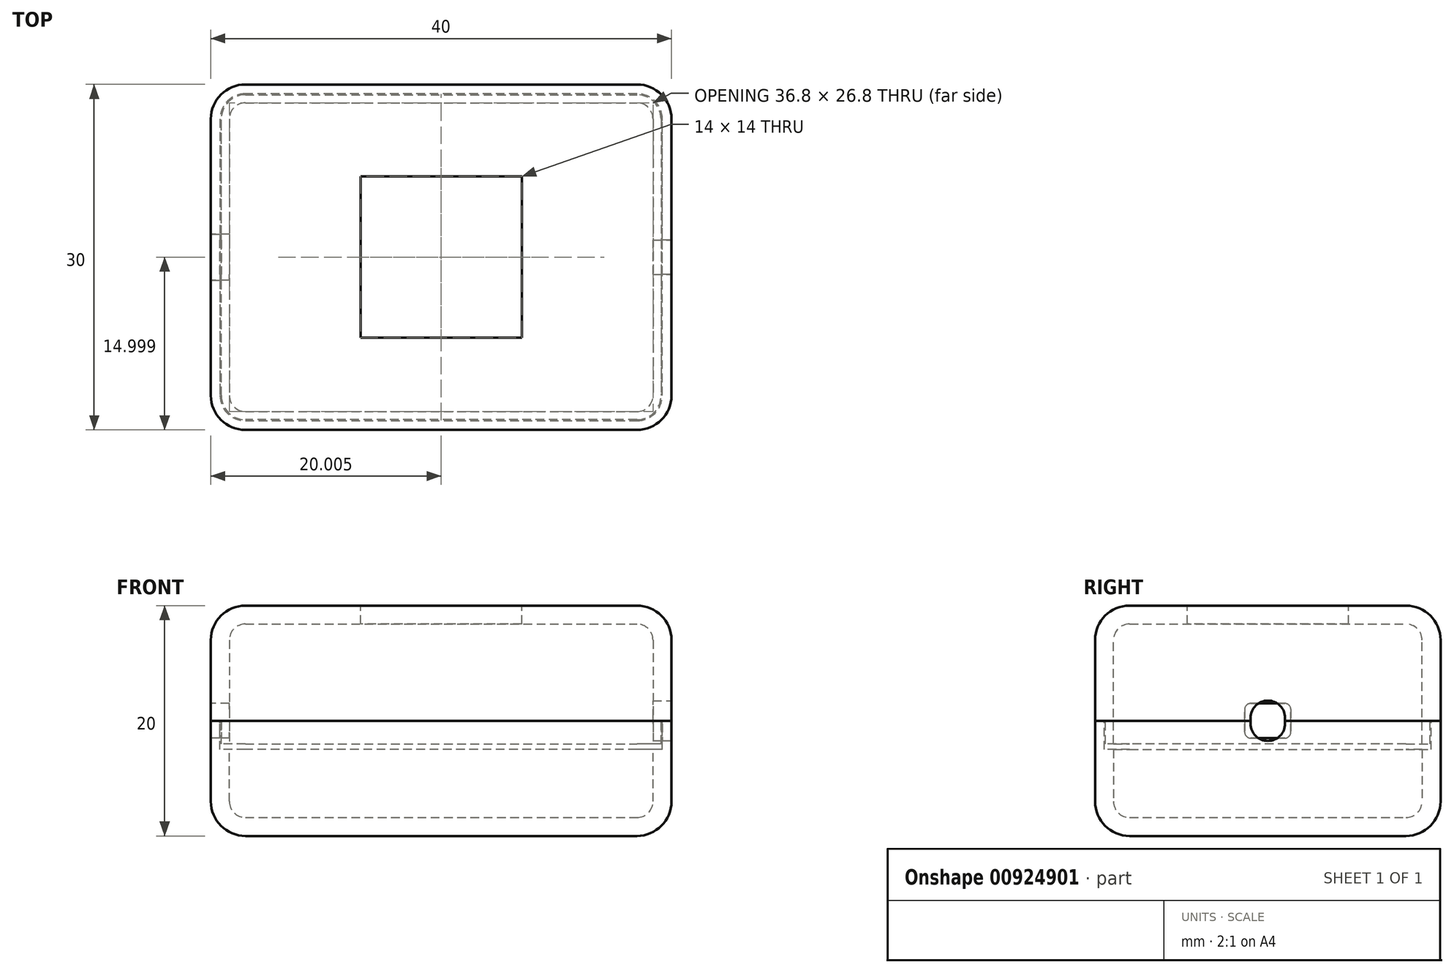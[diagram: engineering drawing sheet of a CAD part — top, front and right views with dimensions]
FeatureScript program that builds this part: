
annotation { "Feature Type Name" : "Feature", "Feature Type Description" : "" }
export const myFeature = defineFeature(function(context is Context, id is Id, definition is map)
    precondition{}
    {
        {
            var Q0;
            Q0=qCreatedBy(makeId("Top.planeOp"),FACE);
            var sketch = newSketch(context, id + "F0", { "sketchPlane" : qUnion([Q0])});
            skLineSegment(sketch, "E0.bottom", {"start": v(-19.45, 19.38) * mm, "end": v(20.55, 19.38) * mm});
            skLineSegment(sketch, "E0.top", {"start": v(-19.45, -10.62) * mm, "end": v(20.55, -10.62) * mm});
            skLineSegment(sketch, "E0.left", {"start": v(-19.45, 19.38) * mm, "end": v(-19.45, -10.62) * mm});
            skLineSegment(sketch, "E0.right", {"start": v(20.55, 19.38) * mm, "end": v(20.55, -10.62) * mm});
            skSolve(sketch);
        }
        {
            var Q0;
            Q0=makeQuery(id+"F0.imprint","IMPRINT",FACE,{"disambiguationData":[TD([[makeQuery(id+"F0.imprint","IMPRINT",EDGE,{"derivedFrom":sQuery(id+"F0.wireOp",EDGE,"6f73b4d0-b99c-471a-bee1-44a85ac8f1db.0")}),1.0]])]});
            var Q1;
            Q1=makeQuery(id+"F0.imprint","IMPRINT",FACE,{"disambiguationData":[TD([[makeQuery(id+"F0.imprint","IMPRINT",EDGE,{"derivedFrom":sQuery(id+"F0.wireOp",EDGE,"E0.bottom")}),-1.0]])]});
            extrude(context, id + "F1", {"entities" : qUnion([Q0, Q1]), "depth" : 10 * mm, "offsetDistance" : 25 * mm});
        }
        {
            var Q0;
            Q0=makeQuery(id+"F1.opExtrude","CAP_FACE",FACE,{"disambiguationData":[OSD([sQuery(id+"F0.wireOp",EDGE,"E0.bottom"),sQuery(id+"F0.wireOp",EDGE,"E0.top"),sQuery(id+"F0.wireOp",EDGE,"E0.left"),sQuery(id+"F0.wireOp",EDGE,"E0.right")])],"isStart":true});
            extrude(context, id + "F2", {"entities" : qUnion([Q0]), "depth" : 10 * mm, "offsetDistance" : 25 * mm});
        }
        {
            var Q0;
            Q0=makeQuery(id+"F2.opExtrude","SWEPT_EDGE",EDGE,{"disambiguationData":[OSD([sQuery(id+"F0.wireOp",EDGE,"E0.top"),sQuery(id+"F0.wireOp",EDGE,"E0.left")])]});
            var Q1;
            Q1=makeQuery(id+"F1.opExtrude","SWEPT_EDGE",EDGE,{"disambiguationData":[OSD([sQuery(id+"F0.wireOp",EDGE,"E0.top"),sQuery(id+"F0.wireOp",EDGE,"E0.left")])]});
            var Q2;
            Q2=makeQuery(id+"F2.opExtrude","SWEPT_EDGE",EDGE,{"disambiguationData":[OSD([sQuery(id+"F0.wireOp",EDGE,"E0.top"),sQuery(id+"F0.wireOp",EDGE,"E0.right")])]});
            var Q3;
            Q3=makeQuery(id+"F1.opExtrude","SWEPT_EDGE",EDGE,{"disambiguationData":[OSD([sQuery(id+"F0.wireOp",EDGE,"E0.top"),sQuery(id+"F0.wireOp",EDGE,"E0.right")])]});
            var Q4;
            Q4=makeQuery(id+"F2.opExtrude","SWEPT_EDGE",EDGE,{"disambiguationData":[OSD([sQuery(id+"F0.wireOp",EDGE,"E0.bottom"),sQuery(id+"F0.wireOp",EDGE,"E0.right")])]});
            var Q5;
            Q5=makeQuery(id+"F1.opExtrude","SWEPT_EDGE",EDGE,{"disambiguationData":[OSD([sQuery(id+"F0.wireOp",EDGE,"E0.bottom"),sQuery(id+"F0.wireOp",EDGE,"E0.right")])]});
            var Q6;
            Q6=makeQuery(id+"F2.opExtrude","SWEPT_EDGE",EDGE,{"disambiguationData":[OSD([sQuery(id+"F0.wireOp",EDGE,"E0.bottom"),sQuery(id+"F0.wireOp",EDGE,"E0.left")])]});
            var Q7;
            Q7=makeQuery(id+"F1.opExtrude","SWEPT_EDGE",EDGE,{"disambiguationData":[OSD([sQuery(id+"F0.wireOp",EDGE,"E0.bottom"),sQuery(id+"F0.wireOp",EDGE,"E0.left")])]});
            var Q8;
            Q8=makeQuery(id+"F2.opExtrude","CAP_EDGE",EDGE,{"disambiguationData":[OSD([sQuery(id+"F0.wireOp",EDGE,"E0.bottom")])],"isStart":false});
            var Q9;
            Q9=makeQuery(id+"F2.opExtrude","CAP_EDGE",EDGE,{"disambiguationData":[OSD([sQuery(id+"F0.wireOp",EDGE,"E0.left")])],"isStart":false});
            var Q10;
            Q10=makeQuery(id+"F2.opExtrude","CAP_EDGE",EDGE,{"disambiguationData":[OSD([sQuery(id+"F0.wireOp",EDGE,"E0.top")])],"isStart":false});
            var Q11;
            Q11=makeQuery(id+"F2.opExtrude","CAP_EDGE",EDGE,{"disambiguationData":[OSD([sQuery(id+"F0.wireOp",EDGE,"E0.right")])],"isStart":false});
            var Q12;
            Q12=makeQuery(id+"F1.opExtrude","CAP_EDGE",EDGE,{"disambiguationData":[OSD([sQuery(id+"F0.wireOp",EDGE,"E0.right")])],"isStart":false});
            var Q13;
            Q13=makeQuery(id+"F1.opExtrude","CAP_EDGE",EDGE,{"disambiguationData":[OSD([sQuery(id+"F0.wireOp",EDGE,"E0.bottom")])],"isStart":false});
            var Q14;
            Q14=makeQuery(id+"F1.opExtrude","CAP_FACE",FACE,{"disambiguationData":[OSD([sQuery(id+"F0.wireOp",EDGE,"E0.bottom"),sQuery(id+"F0.wireOp",EDGE,"E0.top"),sQuery(id+"F0.wireOp",EDGE,"E0.left"),sQuery(id+"F0.wireOp",EDGE,"E0.right")])],"isStart":false});
            fillet(context, id + "F3", {"entities" : qUnion([Q0, Q1, Q2, Q3, Q4, Q5, Q6, Q7, Q8, Q9, Q10, Q11, Q12, Q13, Q14]), "radius" : 3 * mm, "tangentPropagation" : true, "allowEdgeOverflow" : false});
        }
        {
            var Q0;
            Q0=makeQuery(id+"F2.opExtrude","CAP_FACE",FACE,{"disambiguationData":[OSD([sQuery(id+"F0.wireOp",EDGE,"E0.bottom"),sQuery(id+"F0.wireOp",EDGE,"E0.top"),sQuery(id+"F0.wireOp",EDGE,"E0.left"),sQuery(id+"F0.wireOp",EDGE,"E0.right")])],"isStart":true});
            shell(context, id + "F4", {"entities" : qUnion([Q0]), "thickness" : 1.6 * mm});
        }
        {
            var Q0;
            Q0=makeQuery(id+"F1.opExtrude","CAP_FACE",FACE,{"disambiguationData":[OSD([sQuery(id+"F0.wireOp",EDGE,"E0.bottom"),sQuery(id+"F0.wireOp",EDGE,"E0.top"),sQuery(id+"F0.wireOp",EDGE,"E0.left"),sQuery(id+"F0.wireOp",EDGE,"E0.right")])],"isStart":true});
            shell(context, id + "F5", {"entities" : qUnion([Q0]), "thickness" : 1.6 * mm});
        }
        {
            var Q0;
            Q0=makeQuery(id+"F1.opExtrude","CAP_FACE",FACE,{"disambiguationData":[OSD([sQuery(id+"F0.wireOp",EDGE,"E0.bottom"),sQuery(id+"F0.wireOp",EDGE,"E0.top"),sQuery(id+"F0.wireOp",EDGE,"E0.left"),sQuery(id+"F0.wireOp",EDGE,"E0.right")])],"isStart":false});
            var sketch = newSketch(context, id + "F6", { "sketchPlane" : qUnion([Q0])});
            skLineSegment(sketch, "E1.bottom", {"start": v(7.55, 11.38) * mm, "end": v(-6.45, 11.38) * mm});
            skLineSegment(sketch, "E1.top", {"start": v(7.55, -2.62) * mm, "end": v(-6.45, -2.62) * mm});
            skLineSegment(sketch, "E1.left", {"start": v(7.55, 11.38) * mm, "end": v(7.55, -2.62) * mm});
            skLineSegment(sketch, "E1.right", {"start": v(-6.45, 11.38) * mm, "end": v(-6.45, -2.62) * mm});
            skPoint(sketch, "E1.middle", {"position": v(0.55, 4.38) * mm});
            skPoint(sketch, "E1.middle.positionSnap0", {"position": v(17.55, 4.38) * mm});
            skPoint(sketch, "E1.middle.positionSnap1", {"position": v(0.55, 16.38) * mm});
            skPoint(sketch, "E1.centerSnap0", {"position": v(17.55, 4.38) * mm});
            skPoint(sketch, "E1.centerSnap1", {"position": v(0.55, 16.38) * mm});
            skSolve(sketch);
        }
        {
            var Q0;
            Q0=makeQuery(id+"F6.imprint","IMPRINT",FACE,{"disambiguationData":[TD([[makeQuery(id+"F6.imprint","IMPRINT",EDGE,{"derivedFrom":sQuery(id+"F6.wireOp",EDGE,"E1.bottom")}),1.0]])]});
            extrude(context, id + "F7", {"entities" : qUnion([Q0]), "operationType" : NewBodyOperationType.REMOVE, "oppositeDirection" : true, "depth" : 3 * mm, "offsetDistance" : 25 * mm});
        }
        {
            var Q0;
            Q0=makeQuery(id+"F2.opExtrude","CAP_FACE",FACE,{"disambiguationData":[OSD([sQuery(id+"F0.wireOp",EDGE,"E0.bottom"),sQuery(id+"F0.wireOp",EDGE,"E0.top"),sQuery(id+"F0.wireOp",EDGE,"E0.left"),sQuery(id+"F0.wireOp",EDGE,"E0.right")])],"isStart":true});
            var sketch = newSketch(context, id + "F8", { "sketchPlane" : qUnion([Q0])});
            skArc(sketch, "E2.0", {"start": v(19.75, 16.38) * mm, "mid": v(19.11, 17.93) * mm, "end": v(17.55, 18.58) * mm});
            skLineSegment(sketch, "E2.1", {"start": v(19.75, -7.62) * mm, "end": v(19.75, 16.38) * mm});
            skLineSegment(sketch, "E2.2", {"start": v(17.55, 18.58) * mm, "end": v(-16.45, 18.58) * mm});
            skArc(sketch, "E2.3", {"start": v(17.55, -9.82) * mm, "mid": v(19.11, -9.18) * mm, "end": v(19.75, -7.62) * mm});
            skArc(sketch, "E2.4", {"start": v(-16.45, 18.58) * mm, "mid": v(-18, 17.93) * mm, "end": v(-18.65, 16.38) * mm});
            skLineSegment(sketch, "E2.5", {"start": v(-18.65, 16.38) * mm, "end": v(-18.65, -7.62) * mm});
            skArc(sketch, "E2.6", {"start": v(-18.65, -7.62) * mm, "mid": v(-18, -9.18) * mm, "end": v(-16.45, -9.82) * mm});
            skLineSegment(sketch, "E2.7", {"start": v(-16.45, -9.82) * mm, "end": v(17.55, -9.82) * mm});
            skSolve(sketch);
        }
        {
            var Q0;
            Q0=makeQuery(id+"F8.imprint","IMPRINT",FACE,{"disambiguationData":[TD([[makeQuery(id+"F8.imprint","IMPRINT",EDGE,{"derivedFrom":sQuery(id+"F8.wireOp",EDGE,"E2.0")}),1.0]])]});
            extrude(context, id + "F9", {"entities" : qUnion([Q0]), "operationType" : NewBodyOperationType.REMOVE, "oppositeDirection" : true, "depth" : 2.5 * mm, "offsetDistance" : 25 * mm});
        }
        {
            var Q0;
            Q0=makeQuery(id+"F1.opExtrude","CAP_FACE",FACE,{"disambiguationData":[OSD([sQuery(id+"F0.wireOp",EDGE,"E0.bottom"),sQuery(id+"F0.wireOp",EDGE,"E0.top"),sQuery(id+"F0.wireOp",EDGE,"E0.left"),sQuery(id+"F0.wireOp",EDGE,"E0.right")])],"isStart":true});
            var sketch = newSketch(context, id + "F10", { "sketchPlane" : qUnion([Q0])});
            skArc(sketch, "E3.0", {"start": v(19.65, 7.62) * mm, "mid": v(19.04, 9.1) * mm, "end": v(17.55, 9.72) * mm});
            skLineSegment(sketch, "E3.1", {"start": v(19.65, -16.38) * mm, "end": v(19.65, 7.62) * mm});
            skLineSegment(sketch, "E3.2", {"start": v(17.55, 9.72) * mm, "end": v(-16.45, 9.72) * mm});
            skArc(sketch, "E3.3", {"start": v(17.55, -18.48) * mm, "mid": v(19.04, -17.86) * mm, "end": v(19.65, -16.38) * mm});
            skArc(sketch, "E3.4", {"start": v(-16.45, 9.72) * mm, "mid": v(-17.93, 9.1) * mm, "end": v(-18.55, 7.62) * mm});
            skLineSegment(sketch, "E3.5", {"start": v(-18.55, 7.62) * mm, "end": v(-18.55, -16.38) * mm});
            skArc(sketch, "E3.6", {"start": v(-18.55, -16.38) * mm, "mid": v(-17.93, -17.86) * mm, "end": v(-16.45, -18.48) * mm});
            skLineSegment(sketch, "E3.7", {"start": v(-16.45, -18.48) * mm, "end": v(17.55, -18.48) * mm});
            skSolve(sketch);
        }
        {
            var Q0;
            Q0=makeQuery(id+"F10.imprint","IMPRINT",FACE,{"disambiguationData":[TD([[makeQuery(id+"F10.imprint","IMPRINT",EDGE,{"derivedFrom":sQuery(id+"F10.wireOp",EDGE,"E3.0")}),1.0]])]});
            extrude(context, id + "F11", {"entities" : qUnion([Q0]), "operationType" : NewBodyOperationType.ADD, "depth" : 2 * mm, "offsetDistance" : 25 * mm});
        }
        {
            var Q0;
            Q0=makeQuery(id+"F2.opExtrude","SWEPT_FACE",FACE,{"disambiguationData":[OSD([sQuery(id+"F0.wireOp",EDGE,"E0.left")])]});
            var sketch = newSketch(context, id + "F12", { "sketchPlane" : qUnion([Q0])});
            skPoint(sketch, "E4.middle.positionSnap0", {"position": v(7.62, -3.5) * mm});
            skPoint(sketch, "E4.middle.positionSnap1", {"position": v(-4.38, -7) * mm});
            skPoint(sketch, "E4.centerSnap0", {"position": v(7.62, -3.5) * mm});
            skPoint(sketch, "E4.centerSnap1", {"position": v(-4.38, -7) * mm});
            skPoint(sketch, "E5.middle.positionSnap0", {"position": v(-4.38, 0) * mm});
            skPoint(sketch, "E5.centerSnap0", {"position": v(-4.38, 0) * mm});
            skLineSegment(sketch, "E6.bottom", {"start": v(-2.38, -1.5) * mm, "end": v(-6.38, -1.5) * mm});
            skLineSegment(sketch, "E6.top", {"start": v(-2.38, 1.5) * mm, "end": v(-6.38, 1.5) * mm});
            skLineSegment(sketch, "E6.left", {"start": v(-2.38, -1.5) * mm, "end": v(-2.38, 1.5) * mm});
            skLineSegment(sketch, "E6.right", {"start": v(-6.38, -1.5) * mm, "end": v(-6.38, 1.5) * mm});
            skSolve(sketch);
        }
        {
            var Q0;
            {var subQ0=sQuery(id+"F12.wireOp",EDGE,"E6.bottom");Q0=makeQuery(id+"F12.imprint","IMPRINT",FACE,{"disambiguationData":[TD([[makeQuery(id+"F12.imprint","IMPRINT",EDGE,{"derivedFrom":subQ0}),-1.0]])]});}
            var Q1;
            {var subQ0=sQuery(id+"F12.wireOp",EDGE,"E6.top");Q1=makeQuery(id+"F12.imprint","IMPRINT",FACE,{"disambiguationData":[TD([[makeQuery(id+"F12.imprint","IMPRINT",EDGE,{"derivedFrom":subQ0}),1.0]])]});}
            extrude(context, id + "F13", {"entities" : qUnion([Q0, Q1]), "operationType" : NewBodyOperationType.REMOVE, "oppositeDirection" : true, "depth" : 5 * mm, "offsetDistance" : 25 * mm});
        }
        {
            var Q0;
            {var subQ0=sQuery(id+"F12.wireOp",EDGE,"E6.bottom");var subQ1=sQuery(id+"F12.wireOp",EDGE,"E6.right");Q0=makeQuery(id+"F13.boolean.opBoolean","COPY",EDGE,{"disambiguationData":[TD([makeQuery(id+"F2.opExtrude","SWEPT_FACE",FACE,{"disambiguationData":[OSD([sQuery(id+"F0.wireOp",EDGE,"E0.left")])]})])],"derivedFrom":makeQuery(id+"F13.opExtrude","SWEPT_EDGE",EDGE,{"disambiguationData":[OSD([subQ0,subQ1])]})});}
            var Q1;
            {var subQ1=sQuery(id+"F12.wireOp",EDGE,"E6.bottom");var subQ2=sQuery(id+"F12.wireOp",EDGE,"E6.right");Q1=makeQuery(id+"F13.boolean.opBoolean","COPY",EDGE,{"disambiguationData":[TD([makeQuery(id+"F11.opExtrude","SWEPT_FACE",FACE,{"disambiguationData":[OSD([sQuery(id+"F10.wireOp",EDGE,"E3.5")])]})])],"derivedFrom":makeQuery(id+"F13.opExtrude","SWEPT_EDGE",EDGE,{"disambiguationData":[OSD([subQ1,subQ2])]})});}
            var Q2;
            {var subQ0=sQuery(id+"F12.wireOp",EDGE,"E6.left");var subQ1=sQuery(id+"F12.wireOp",EDGE,"E6.bottom");Q2=makeQuery(id+"F13.boolean.opBoolean","COPY",EDGE,{"disambiguationData":[TD([makeQuery(id+"F2.opExtrude","SWEPT_FACE",FACE,{"disambiguationData":[OSD([sQuery(id+"F0.wireOp",EDGE,"E0.left")])]})])],"derivedFrom":makeQuery(id+"F13.opExtrude","SWEPT_EDGE",EDGE,{"disambiguationData":[OSD([subQ1,subQ0])]})});}
            var Q3;
            {var subQ1=sQuery(id+"F12.wireOp",EDGE,"E6.bottom");var subQ2=sQuery(id+"F12.wireOp",EDGE,"E6.left");Q3=makeQuery(id+"F13.boolean.opBoolean","COPY",EDGE,{"disambiguationData":[TD([makeQuery(id+"F11.opExtrude","SWEPT_FACE",FACE,{"disambiguationData":[OSD([sQuery(id+"F10.wireOp",EDGE,"E3.5")])]})])],"derivedFrom":makeQuery(id+"F13.opExtrude","SWEPT_EDGE",EDGE,{"disambiguationData":[OSD([subQ1,subQ2])]})});}
            var Q4;
            Q4=makeQuery(id+"F13.boolean.opBoolean","COPY",EDGE,{"derivedFrom":makeQuery(id+"F13.opExtrude","SWEPT_EDGE",EDGE,{"disambiguationData":[OSD([sQuery(id+"F12.wireOp",EDGE,"E6.top"),sQuery(id+"F12.wireOp",EDGE,"E6.right")])]})});
            var Q5;
            Q5=makeQuery(id+"F13.boolean.opBoolean","COPY",EDGE,{"derivedFrom":makeQuery(id+"F13.opExtrude","SWEPT_EDGE",EDGE,{"disambiguationData":[OSD([sQuery(id+"F12.wireOp",EDGE,"E6.top"),sQuery(id+"F12.wireOp",EDGE,"E6.left")])]})});
            fillet(context, id + "F14", {"entities" : qUnion([Q0, Q1, Q2, Q3, Q4, Q5]), "radius" : 0.5 * mm, "tangentPropagation" : true, "allowEdgeOverflow" : false});
        }
        {
            var Q0;
            Q0=makeQuery(id+"F1.opExtrude","SWEPT_FACE",FACE,{"disambiguationData":[OSD([sQuery(id+"F0.wireOp",EDGE,"E0.right")])]});
            var sketch = newSketch(context, id + "F15", { "sketchPlane" : qUnion([Q0])});
            skLineSegment(sketch, "E7.bottom", {"start": v(5.88, -1.75) * mm, "end": v(2.88, -1.75) * mm});
            skLineSegment(sketch, "E7.top", {"start": v(5.88, 1.75) * mm, "end": v(2.88, 1.75) * mm});
            skLineSegment(sketch, "E7.left", {"start": v(5.88, -1.75) * mm, "end": v(5.88, 1.75) * mm});
            skLineSegment(sketch, "E7.right", {"start": v(2.88, -1.75) * mm, "end": v(2.88, 1.75) * mm});
            skPoint(sketch, "E7.middle", {"position": v(4.38, 0) * mm});
            skSolve(sketch);
        }
        {
            var Q0;
            {var subQ0=sQuery(id+"F15.wireOp",EDGE,"E7.top");Q0=makeQuery(id+"F15.imprint","IMPRINT",FACE,{"disambiguationData":[TD([[makeQuery(id+"F15.imprint","IMPRINT",EDGE,{"derivedFrom":subQ0}),1.0]])]});}
            var Q1;
            {var subQ0=sQuery(id+"F15.wireOp",EDGE,"E7.bottom");Q1=makeQuery(id+"F15.imprint","IMPRINT",FACE,{"disambiguationData":[TD([[makeQuery(id+"F15.imprint","IMPRINT",EDGE,{"derivedFrom":subQ0}),-1.0]])]});}
            extrude(context, id + "F16", {"entities" : qUnion([Q0, Q1]), "operationType" : NewBodyOperationType.REMOVE, "oppositeDirection" : true, "depth" : 5 * mm, "offsetDistance" : 25 * mm});
        }
        {
            var Q0;
            {var subQ0=sQuery(id+"F15.wireOp",EDGE,"E7.bottom");var subQ2=sQuery(id+"F15.wireOp",EDGE,"E7.right");Q0=makeQuery(id+"F16.boolean.opBoolean","COPY",EDGE,{"disambiguationData":[TD([makeQuery(id+"F11.opExtrude","SWEPT_FACE",FACE,{"disambiguationData":[OSD([sQuery(id+"F10.wireOp",EDGE,"E3.1")])]})])],"derivedFrom":makeQuery(id+"F16.opExtrude","SWEPT_EDGE",EDGE,{"disambiguationData":[OSD([subQ0,subQ2])]})});}
            var Q1;
            {var subQ0=sQuery(id+"F15.wireOp",EDGE,"E7.bottom");var subQ1=sQuery(id+"F15.wireOp",EDGE,"E7.right");Q1=makeQuery(id+"F16.boolean.opBoolean","COPY",EDGE,{"disambiguationData":[TD([makeQuery(id+"F2.opExtrude","SWEPT_FACE",FACE,{"disambiguationData":[OSD([sQuery(id+"F0.wireOp",EDGE,"E0.right")])]})])],"derivedFrom":makeQuery(id+"F16.opExtrude","SWEPT_EDGE",EDGE,{"disambiguationData":[OSD([subQ0,subQ1])]})});}
            var Q2;
            {var subQ0=sQuery(id+"F15.wireOp",EDGE,"E7.bottom");var subQ2=sQuery(id+"F15.wireOp",EDGE,"E7.left");Q2=makeQuery(id+"F16.boolean.opBoolean","COPY",EDGE,{"disambiguationData":[TD([makeQuery(id+"F11.opExtrude","SWEPT_FACE",FACE,{"disambiguationData":[OSD([sQuery(id+"F10.wireOp",EDGE,"E3.1")])]})])],"derivedFrom":makeQuery(id+"F16.opExtrude","SWEPT_EDGE",EDGE,{"disambiguationData":[OSD([subQ0,subQ2])]})});}
            var Q3;
            {var subQ0=sQuery(id+"F15.wireOp",EDGE,"E7.bottom");var subQ1=sQuery(id+"F15.wireOp",EDGE,"E7.left");Q3=makeQuery(id+"F16.boolean.opBoolean","COPY",EDGE,{"disambiguationData":[TD([makeQuery(id+"F2.opExtrude","SWEPT_FACE",FACE,{"disambiguationData":[OSD([sQuery(id+"F0.wireOp",EDGE,"E0.right")])]})])],"derivedFrom":makeQuery(id+"F16.opExtrude","SWEPT_EDGE",EDGE,{"disambiguationData":[OSD([subQ0,subQ1])]})});}
            var Q4;
            Q4=makeQuery(id+"F16.boolean.opBoolean","COPY",EDGE,{"derivedFrom":makeQuery(id+"F16.opExtrude","SWEPT_EDGE",EDGE,{"disambiguationData":[OSD([sQuery(id+"F15.wireOp",EDGE,"E7.top"),sQuery(id+"F15.wireOp",EDGE,"E7.right")])]})});
            var Q5;
            Q5=makeQuery(id+"F16.boolean.opBoolean","COPY",EDGE,{"derivedFrom":makeQuery(id+"F16.opExtrude","SWEPT_EDGE",EDGE,{"disambiguationData":[OSD([sQuery(id+"F15.wireOp",EDGE,"E7.top"),sQuery(id+"F15.wireOp",EDGE,"E7.left")])]})});
            fillet(context, id + "F17", {"entities" : qUnion([Q0, Q1, Q2, Q3, Q4, Q5]), "radius" : 1.5 * mm, "tangentPropagation" : true, "allowEdgeOverflow" : false});
        }
    });
